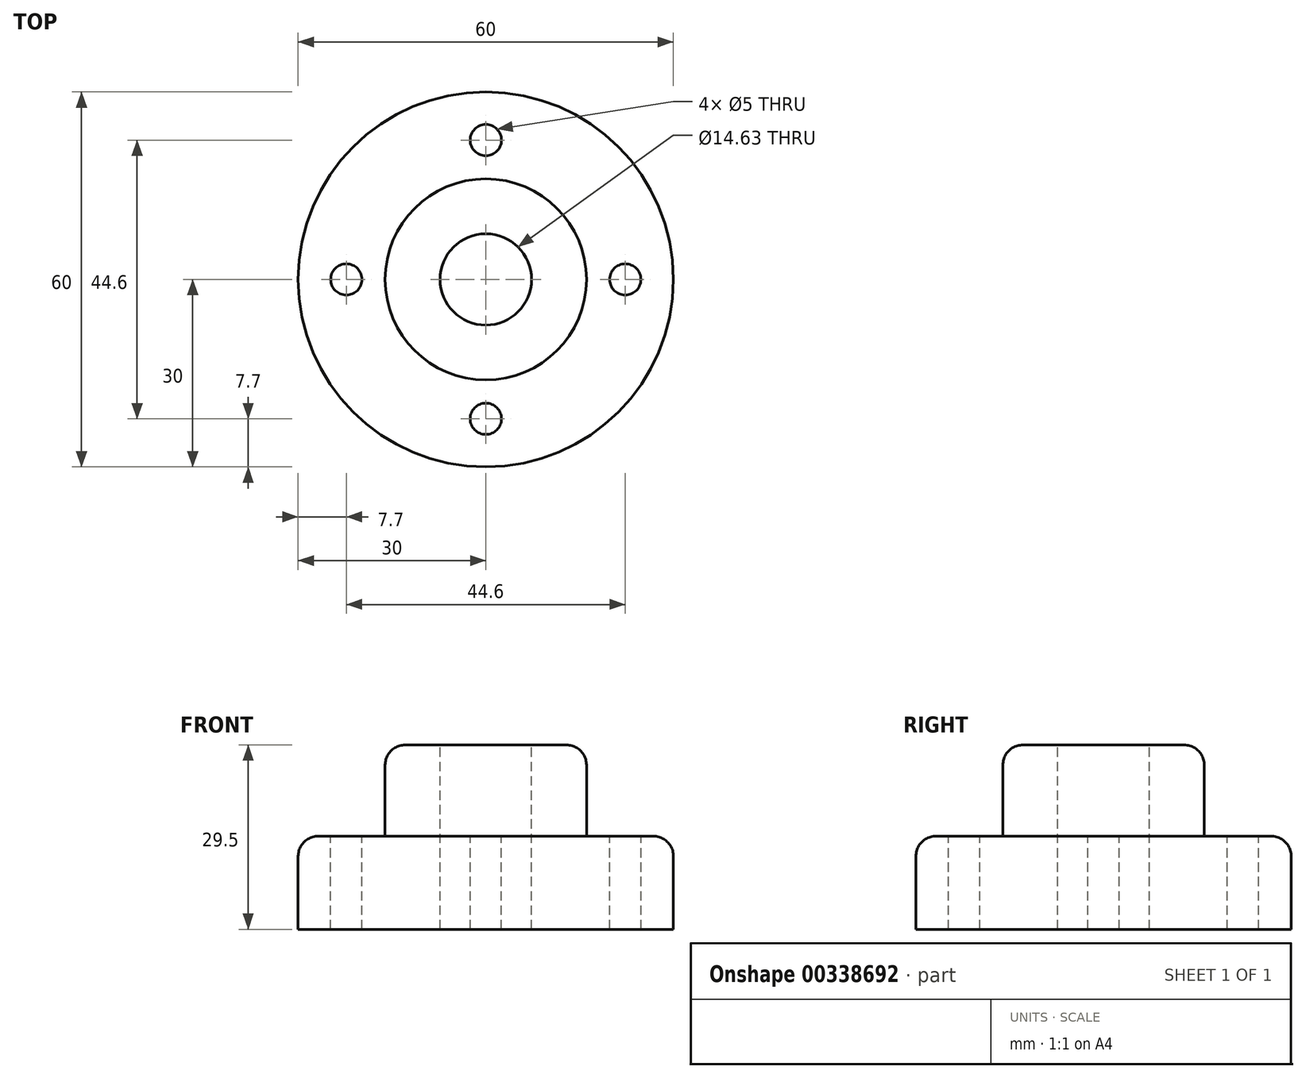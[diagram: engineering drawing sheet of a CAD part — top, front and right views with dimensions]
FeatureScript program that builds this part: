
annotation { "Feature Type Name" : "Feature", "Feature Type Description" : "" }
export const myFeature = defineFeature(function(context is Context, id is Id, definition is map)
    precondition{}
    {
        {
            var Q0;
            Q0=qCreatedBy(makeId("Top.planeOp"),FACE);
            var sketch = newSketch(context, id + "F0", { "sketchPlane" : qUnion([Q0])});
            skCircle(sketch, "E0", {"center": v(0, 0) * mm, "radius": 30 * mm});
            skSolve(sketch);
        }
        {
            var Q0;
            Q0=qSketchRegion(id+"F0",true);
            extrude(context, id + "F1", {"entities" : qUnion([Q0]), "depth" : 14.9 * mm});
        }
        {
            var Q0;
            Q0=makeQuery(id+"F1.opExtrude","CAP_FACE",FACE,{"disambiguationData":[OSD([sQuery(id+"F0.wireOp",EDGE,"E0")])],"isStart":false});
            cPlane(context, id + "F2", {"entities" : qUnion([Q0]), "cplaneType" : CPlaneType.OFFSET, "offset" : 0 * mm, "width" : 150 * mm, "height" : 150 * mm});
        }
        {
            var Q0;
            Q0=qCreatedBy(id+"F2.planeOp",FACE);
            var sketch = newSketch(context, id + "F3", { "sketchPlane" : qUnion([Q0])});
            skCircle(sketch, "E1", {"center": v(0, 0) * mm, "radius": 16.1 * mm});
            skSolve(sketch);
        }
        {
            var Q0;
            Q0=qSketchRegion(id+"F3",true);
            extrude(context, id + "F4", {"entities" : qUnion([Q0]), "operationType" : NewBodyOperationType.ADD, "depth" : 14.6 * mm});
        }
        {
            var Q0;
            Q0=qCreatedBy(id+"F2.planeOp",FACE);
            var sketch = newSketch(context, id + "F5", { "sketchPlane" : qUnion([Q0])});
            skCircle(sketch, "E2", {"center": v(-22.3, 0) * mm, "radius": 2.5 * mm});
            skCircle(sketch, "E3", {"center": v(0, 22.3) * mm, "radius": 2.5 * mm});
            skCircle(sketch, "E4", {"center": v(22.3, 0) * mm, "radius": 2.5 * mm});
            skCircle(sketch, "E5", {"center": v(0, -22.3) * mm, "radius": 2.5 * mm});
            skSolve(sketch);
        }
        {
            var Q0;
            Q0=qSketchRegion(id+"F5",true);
            extrude(context, id + "F6", {"entities" : qUnion([Q0]), "operationType" : NewBodyOperationType.REMOVE, "oppositeDirection" : true, "depth" : 25 * mm});
        }
        {
            var Q0;
            Q0=makeQuery(id+"F1.opExtrude","CAP_EDGE",EDGE,{"disambiguationData":[OSD([sQuery(id+"F0.wireOp",EDGE,"E0")])],"isStart":false});
            var Q1;
            Q1=makeQuery(id+"F4.opExtrude","CAP_EDGE",EDGE,{"disambiguationData":[OSD([sQuery(id+"F3.wireOp",EDGE,"E1")])],"isStart":false});
            fillet(context, id + "F7", {"entities" : qUnion([Q0, Q1]), "radius" : 3.2 * mm, "tangentPropagation" : true, "allowEdgeOverflow" : false});
        }
        {
            var Q0;
            Q0=makeQuery(id+"F4.opExtrude","CAP_FACE",FACE,{"disambiguationData":[OSD([sQuery(id+"F3.wireOp",EDGE,"E1")])],"isStart":false});
            cPlane(context, id + "F8", {"entities" : qUnion([Q0]), "cplaneType" : CPlaneType.OFFSET, "offset" : 0 * mm, "width" : 150 * mm, "height" : 150 * mm});
        }
        {
            var Q0;
            Q0=qCreatedBy(id+"F8.planeOp",FACE);
            var sketch = newSketch(context, id + "F9", { "sketchPlane" : qUnion([Q0])});
            skCircle(sketch, "E6", {"center": v(0, 0) * mm, "radius": 7.32 * mm});
            skSolve(sketch);
        }
        {
            var Q0;
            Q0=qSketchRegion(id+"F9",true);
            extrude(context, id + "F10", {"entities" : qUnion([Q0]), "operationType" : NewBodyOperationType.REMOVE, "oppositeDirection" : true, "depth" : 50 * mm});
        }
    });
